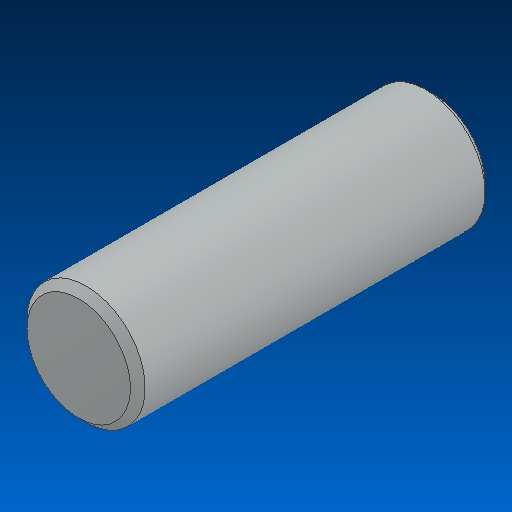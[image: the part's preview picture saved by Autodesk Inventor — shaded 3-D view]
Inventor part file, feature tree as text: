
AUTODESK INVENTOR PART (.ipt)
format: ipt  version: 2022.2 (Build 262287000, 287)  size: 103,424 bytes
history: native  units: in
note: dims shown in document units (in); Inventor stores cm internally (conversion verified against a paired STEP export)
features: chamfer x1
ambient origin geometry x8: Origin, YZ Plane, XZ Plane, XY Plane, X Axis, Y Axis, Z Axis, Center Point
bodies: Solid1 (feature_tree)
feature tree (1):
  chamfer  "Chamfer1"  [1 undecoded]
note: 1 required parameter value undecoded (feature->parameter linkage not recoverable at this tier; creation-order binding heuristic only, values carry confidence <= 0.55)
